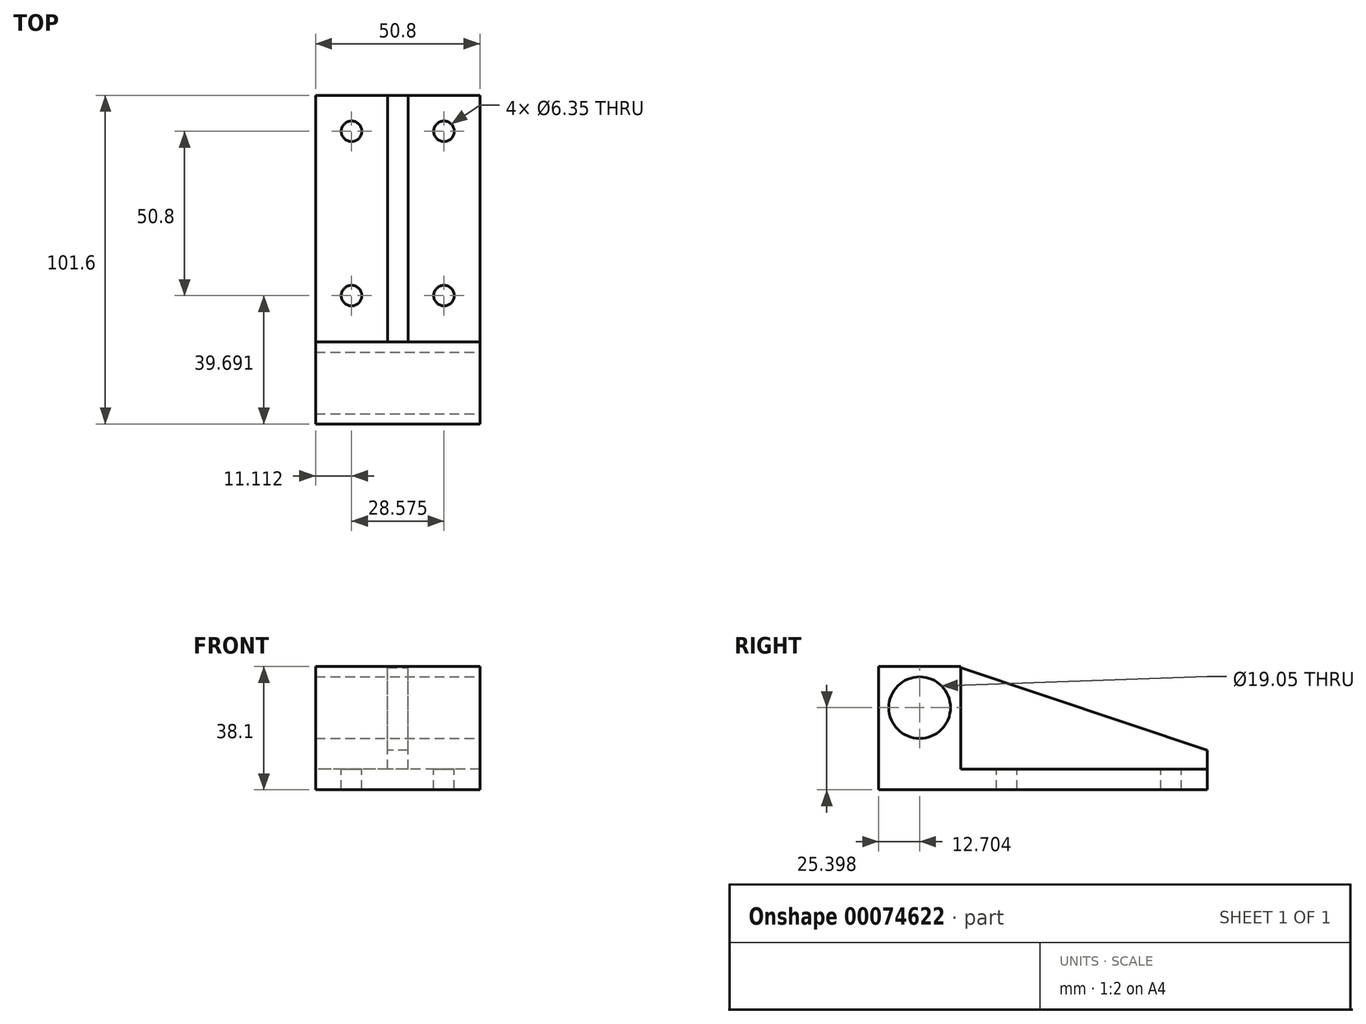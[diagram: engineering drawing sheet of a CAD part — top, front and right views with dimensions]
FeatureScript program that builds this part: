
annotation { "Feature Type Name" : "Feature", "Feature Type Description" : "" }
export const myFeature = defineFeature(function(context is Context, id is Id, definition is map)
    precondition{}
    {
        {
            var Q0;
            Q0=qCreatedBy(makeId("Right.planeOp"),FACE);
            var sketch = newSketch(context, id + "F0", { "sketchPlane" : qUnion([Q0])});
            skLineSegment(sketch, "E0", {"start": v(-31.1, 18.96) * mm, "end": v(-31.1, -19.14) * mm});
            skLineSegment(sketch, "E1", {"start": v(-31.1, -19.14) * mm, "end": v(70.5, -19.14) * mm});
            skLineSegment(sketch, "E2", {"start": v(70.5, -19.14) * mm, "end": v(70.5, -12.8) * mm});
            skLineSegment(sketch, "E3", {"start": v(70.5, -12.8) * mm, "end": v(-5.7, -12.8) * mm});
            skLineSegment(sketch, "E4", {"start": v(-5.7, -12.8) * mm, "end": v(-5.7, 18.96) * mm});
            skLineSegment(sketch, "E5", {"start": v(-5.7, 18.96) * mm, "end": v(-31.1, 18.96) * mm});
            skSolve(sketch);
        }
        {
            var Q0;
            Q0=makeQuery(id+"F0.imprint","IMPRINT",FACE,{"disambiguationData":[TD([[makeQuery(id+"F0.imprint","IMPRINT",EDGE,{"derivedFrom":sQuery(id+"F0.wireOp",EDGE,"E0")}),1.0]])]});
            extrude(context, id + "F1", {"entities" : qUnion([Q0]), "depth" : 25.4 * mm, "hasSecondDirection" : true, "secondDirectionOppositeDirection" : true, "secondDirectionDepth" : 25.4 * mm});
        }
        {
            var Q0;
            Q0=makeQuery(id+"F1.opExtrude","SWEPT_FACE",FACE,{"disambiguationData":[OSD([sQuery(id+"F0.wireOp",EDGE,"E3")])]});
            var sketch = newSketch(context, id + "F2", { "sketchPlane" : qUnion([Q0])});
            skLineSegment(sketch, "E6.rect.bottom", {"start": v(-3.17, 70.5) * mm, "end": v(3.18, 70.5) * mm});
            skLineSegment(sketch, "E6.rect.top", {"start": v(-3.17, -5.7) * mm, "end": v(3.18, -5.7) * mm});
            skLineSegment(sketch, "E6.rect.left", {"start": v(-3.17, 70.5) * mm, "end": v(-3.17, -5.7) * mm});
            skLineSegment(sketch, "E6.rect.right", {"start": v(3.18, 70.5) * mm, "end": v(3.18, -5.7) * mm});
            skPoint(sketch, "E6.rect.middle", {"position": v(0, 32.4) * mm});
            skSolve(sketch);
        }
        {
            var Q0;
            Q0=qCreatedBy(makeId("Right.planeOp"),FACE);
            var sketch = newSketch(context, id + "F3", { "sketchPlane" : qUnion([Q0])});
            skLineSegment(sketch, "E7", {"start": v(70.48, -13.23) * mm, "end": v(70.48, -6.88) * mm});
            skLineSegment(sketch, "E8", {"start": v(70.48, -6.88) * mm, "end": v(-5.92, 18.71) * mm});
            skLineSegment(sketch, "E9", {"start": v(-5.92, 18.71) * mm, "end": v(-5.92, -13.26) * mm});
            skLineSegment(sketch, "E10", {"start": v(-5.92, -13.26) * mm, "end": v(70.48, -13.23) * mm});
            skSolve(sketch);
        }
        {
            var Q0;
            Q0 = qSketchRegion(id + "F3", true);
            extrude(context, id + "F4", {"entities" : qUnion([Q0]), "operationType" : NewBodyOperationType.ADD, "depth" : 3.17 * mm, "hasSecondDirection" : true, "secondDirectionOppositeDirection" : true, "secondDirectionDepth" : 3.17 * mm});
        }
        {
            var Q0;
            Q0=makeQuery(id+"F1.opExtrude","CAP_FACE",FACE,{"disambiguationData":[OSD([sQuery(id+"F0.wireOp",EDGE,"E0"),sQuery(id+"F0.wireOp",EDGE,"E1"),sQuery(id+"F0.wireOp",EDGE,"E2"),sQuery(id+"F0.wireOp",EDGE,"E3"),sQuery(id+"F0.wireOp",EDGE,"E4"),sQuery(id+"F0.wireOp",EDGE,"E5")])],"isStart":false});
            var sketch = newSketch(context, id + "F5", { "sketchPlane" : qUnion([Q0])});
            skPoint(sketch, "E11", {"position": v(-18.4, 6.26) * mm});
            skSolve(sketch);
        }
        {
            var Q0;
            Q0=sQuery(id+"F5.wireOp",VERTEX,"E11");
            var Q1;
            Q1=makeQuery(id+"F1.opExtrude","SWEPT_BODY",BODY,{"disambiguationData":[OSD([sQuery(id+"F0.wireOp",EDGE,"E0"),sQuery(id+"F0.wireOp",EDGE,"E1"),sQuery(id+"F0.wireOp",EDGE,"E2"),sQuery(id+"F0.wireOp",EDGE,"E3"),sQuery(id+"F0.wireOp",EDGE,"E4"),sQuery(id+"F0.wireOp",EDGE,"E5")])]});
            hole(context, id + "F6", {"style" : HoleStyle.SIMPLE, "holeDiameter" : 19.05 * mm, "endStyle" : HoleEndStyle.THROUGH, "locations" : qUnion([Q0]), "scope" : qUnion([Q1])});
        }
        {
            var Q0;
            {var subQ0=sQuery(id+"F2.wireOp",EDGE,"E6.rect.right");Q0=makeQuery(id+"F2.imprint","IMPRINT",FACE,{"disambiguationData":[TD([[makeQuery(id+"F2.imprint","IMPRINT",EDGE,{"derivedFrom":subQ0}),1.0]])]});}
            var sketch = newSketch(context, id + "F7", { "sketchPlane" : qUnion([Q0])});
            skPoint(sketch, "E12", {"position": v(14.29, 59.4) * mm});
            skPoint(sketch, "E13", {"position": v(14.29, 8.6) * mm});
            skPoint(sketch, "E14.MirrorP", {"position": v(-14.29, 8.6) * mm});
            skPoint(sketch, "E15.MirrorP", {"position": v(-14.29, 59.4) * mm});
            skSolve(sketch);
        }
        {
            var Q0;
            Q0=sQuery(id+"F7.wireOp",VERTEX,"E14.MirrorP");
            var Q1;
            Q1=sQuery(id+"F7.wireOp",VERTEX,"E15.MirrorP");
            var Q2;
            Q2=sQuery(id+"F7.wireOp",VERTEX,"E13");
            var Q3;
            Q3=sQuery(id+"F7.wireOp",VERTEX,"E12");
            var Q4;
            Q4=makeQuery(id+"F1.opExtrude","SWEPT_BODY",BODY,{"disambiguationData":[OSD([sQuery(id+"F0.wireOp",EDGE,"E0"),sQuery(id+"F0.wireOp",EDGE,"E1"),sQuery(id+"F0.wireOp",EDGE,"E2"),sQuery(id+"F0.wireOp",EDGE,"E3"),sQuery(id+"F0.wireOp",EDGE,"E4"),sQuery(id+"F0.wireOp",EDGE,"E5")])]});
            hole(context, id + "F8", {"style" : HoleStyle.SIMPLE, "holeDiameter" : 6.35 * mm, "endStyle" : HoleEndStyle.THROUGH, "locations" : qUnion([Q0, Q1, Q2, Q3]), "scope" : qUnion([Q4])});
        }
    });
